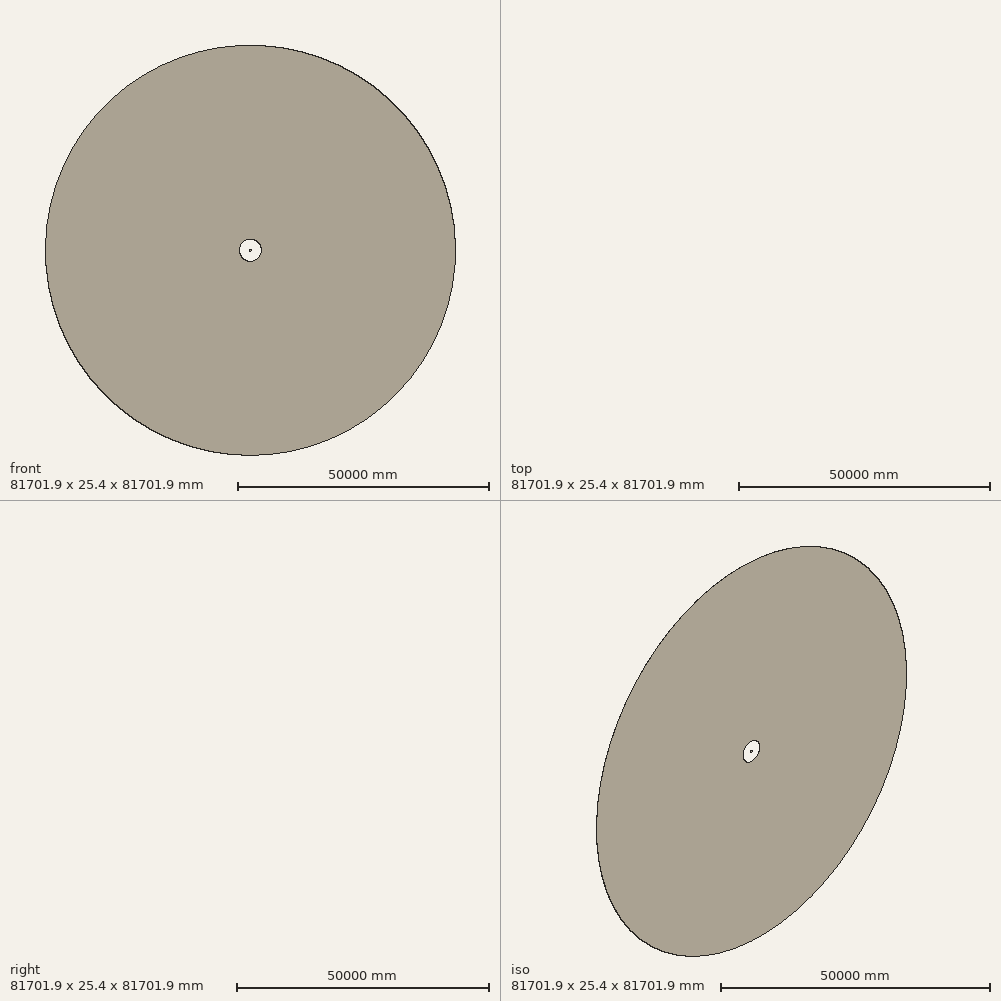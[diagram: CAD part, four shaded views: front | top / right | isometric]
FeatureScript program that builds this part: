
annotation { "Feature Type Name" : "Feature", "Feature Type Description" : "" }
export const myFeature = defineFeature(function(context is Context, id is Id, definition is map)
    precondition{}
    {
        {
            var Q0;
            Q0=qCreatedBy(makeId("Front.planeOp"),FACE);
            var sketch = newSketch(context, id + "F0", { "sketchPlane" : qUnion([Q0])});
            skLineSegment(sketch, "E0.bottom", {"start": v(-190.5, 177.8) * mm, "end": v(190.5, 177.8) * mm});
            skLineSegment(sketch, "E0.top", {"start": v(-190.5, -177.8) * mm, "end": v(190.5, -177.8) * mm});
            skLineSegment(sketch, "E0.left", {"start": v(-190.5, 177.8) * mm, "end": v(-190.5, -177.8) * mm});
            skLineSegment(sketch, "E0.right", {"start": v(190.5, 177.8) * mm, "end": v(190.5, -177.8) * mm});
            skPoint(sketch, "E0.middle", {"position": v(0, 0) * mm});
            skCircle(sketch, "E1", {"center": v(0, 0) * mm, "radius": 2192.97 * mm});
            skCircle(sketch, "E2", {"center": v(0, 0) * mm, "radius": 8911.01 * mm});
            skCircle(sketch, "E3", {"center": v(0, 0) * mm, "radius": 40850.94 * mm});
            skSolve(sketch);
        }
        {
            var Q0;
            Q0 = qSketchRegion(id + "F0", true);
            var Q1;
            Q1=makeQuery(id+"F0.imprint","IMPRINT",FACE,{"disambiguationData":[TD([[makeQuery(id+"F0.imprint","IMPRINT",EDGE,{"derivedFrom":sQuery(id+"F0.wireOp",EDGE,"E1")}),-1.0]])]});
            var Q2;
            Q2=makeQuery(id+"F0.imprint","IMPRINT",FACE,{"disambiguationData":[TD([[makeQuery(id+"F0.imprint","IMPRINT",EDGE,{"derivedFrom":sQuery(id+"F0.wireOp",EDGE,"E0.bottom")}),-1.0]])]});
            extrude(context, id + "F1", {"entities" : qUnion([Q0, Q1, Q2]), "depth" : 25.4 * mm});
        }
    });
